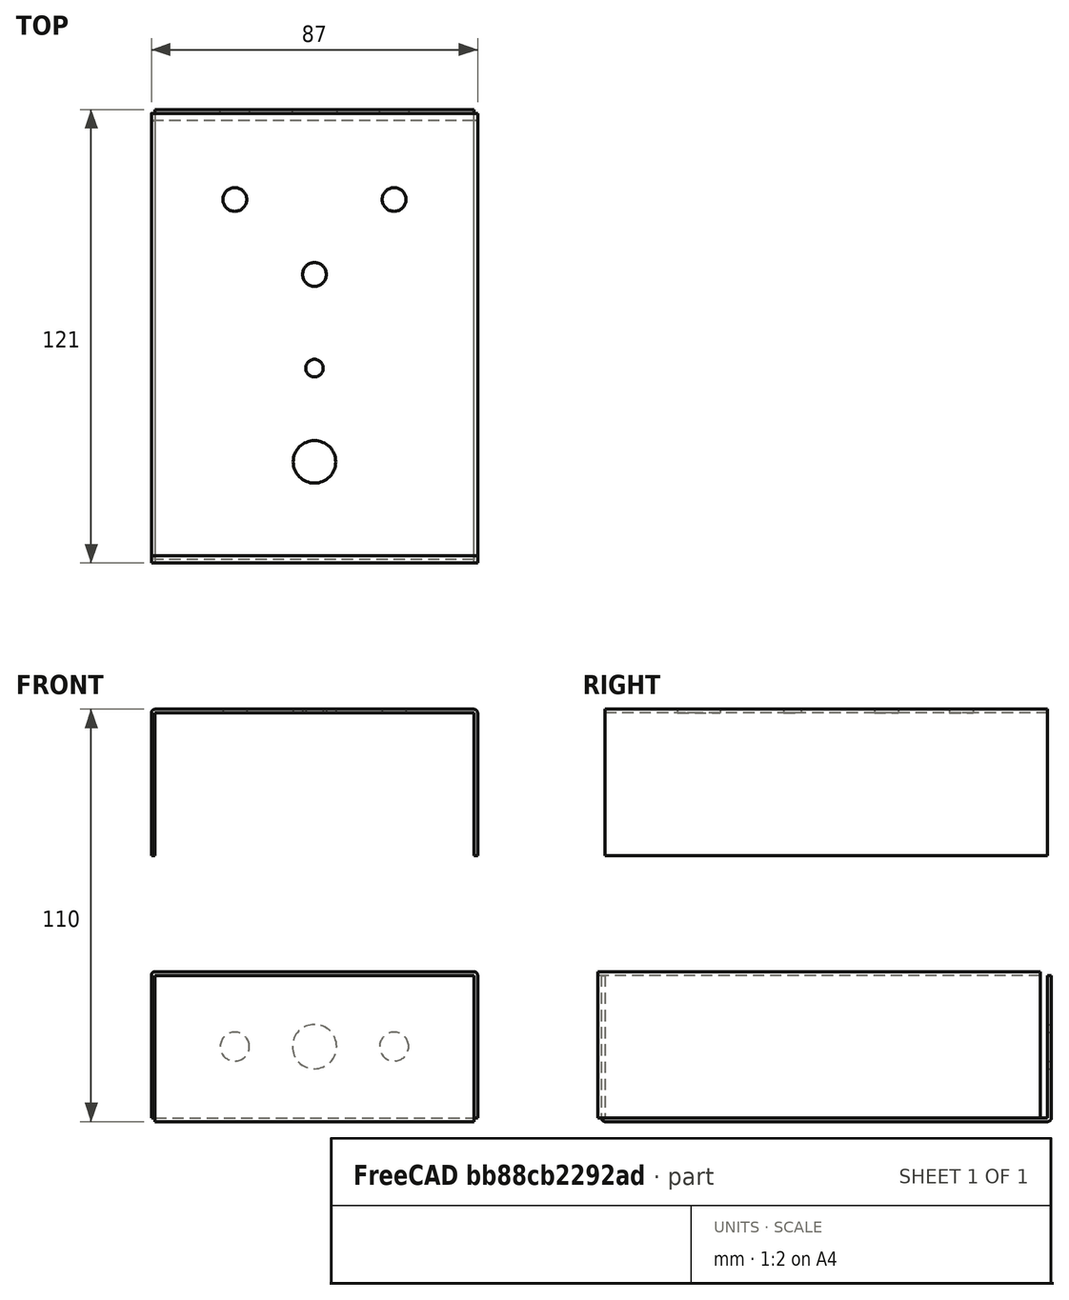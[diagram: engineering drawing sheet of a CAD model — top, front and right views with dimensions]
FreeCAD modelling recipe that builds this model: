
FCSTD DOCUMENT  (FreeCAD 0.21R33771 (Git))
Label: Trino1
License: All rights reserved
LicenseURL: http://en.wikipedia.org/wiki/All_rights_reserved
objects: TechDraw::DrawViewDimension×20, TechDraw::DrawProjGroupItem×14, Sketcher::SketchObject×5, PartDesign::Pad×3, PartDesign::Thickness×3, PartDesign::Body×3, PartDesign::Hole×3, TechDraw::DrawSVGTemplate×2, TechDraw::DrawProjGroup×2, TechDraw::DrawPage×2, PartDesign::ShapeBinder×1, App::FeaturePython×1, PartDesign::Pocket×1
note: 61 computed .brp shape members not serialized (recipe doc carries the construction recipe); baked Part::Feature solids carry a one-line shape summary decoded from their .brp

FEATURE [Sketcher::SketchObject] Sketch
  FullyConstrained = true
  MapMode = 5
  Support = -> [XY_Plane]
  sketch-geometry (4):
    g0: LineSegment StartX=0 StartY=118 StartZ=0 EndX=0 EndY=0 EndZ=0
    g1: LineSegment StartX=0 StartY=0 StartZ=0 EndX=85 EndY=0 EndZ=0
    g2: LineSegment StartX=85 StartY=0 StartZ=0 EndX=85 EndY=118 EndZ=0
    g3: LineSegment StartX=85 StartY=118 StartZ=0 EndX=0 EndY=118 EndZ=0
  constraints (11):
    c: Coincident(g0,g1)
    c: Coincident(g1,g2)
    c: Vertical(g2)
    c: Coincident(g2,g3)
    c: Coincident(g3,g0)
    c: Vertical(g0)
    c: Horizontal(g3)
    c: Horizontal(g1)
    c: DistanceY(g2,g2) = 118
    c: DistanceX(g3,g3) = 85
    c: Coincident(g0,g-1)
FEATURE [PartDesign::Pad] Pad
  Direction = (0,0,1)
  Length = 38
  Length2 = 10
  Profile = -> Sketch
  ReferenceAxis = -> Sketch [N_Axis]
  Type = 0
FEATURE [Sketcher::SketchObject] Sketch002
  FullyConstrained = true
  MapMode = 5
  Support = -> [XY_Plane001]
  sketch-geometry (4):
    g0: LineSegment StartX=0 StartY=118 StartZ=0 EndX=0 EndY=0 EndZ=0
    g1: LineSegment StartX=0 StartY=0 StartZ=0 EndX=85 EndY=0 EndZ=0
    g2: LineSegment StartX=85 StartY=0 StartZ=0 EndX=85 EndY=118 EndZ=0
    g3: LineSegment StartX=85 StartY=118 StartZ=0 EndX=0 EndY=118 EndZ=0
  constraints (11):
    c: Coincident(g0,g1)
    c: Coincident(g1,g2)
    c: Vertical(g2)
    c: Coincident(g2,g3)
    c: Coincident(g3,g0)
    c: Vertical(g0)
    c: Horizontal(g3)
    c: Horizontal(g1)
    c: DistanceY(g2,g2) = 118
    c: DistanceX(g3,g3) = 85
    c: Coincident(g0,g-1)
FEATURE [PartDesign::Pad] Pad001
  Direction = (0,0,1)
  Length = 38
  Length2 = 10
  Profile = -> Sketch002
  ReferenceAxis = -> Sketch002 [N_Axis]
  Type = 0
FEATURE [PartDesign::Thickness] Thickness001
  Base = -> Pad001 [Face3,Face5,Face1]
  BaseFeature = -> Pad001
  Intersection = false
  Join = 0
  Mode = 0
  SupportTransform = false
  Value = 1
FEATURE [PartDesign::ShapeBinder] CopyThickness
  Placement = pos=(0,0,38) rot=(0,0,1;0rad)
  TraceSupport = false
FEATURE [PartDesign::Thickness] Thickness
  Base = -> Pad [Face4,Face5,Face2]
  BaseFeature = -> Pad
  Intersection = false
  Join = 0
  Mode = 0
  SupportTransform = false
  Value = 1
FEATURE [Sketcher::SketchObject] Sketch006
  FullyConstrained = true
  MapMode = 5
  Support = -> [XY_Plane002]
  sketch-geometry (4):
    g0: LineSegment StartX=0 StartY=118 StartZ=0 EndX=0 EndY=0 EndZ=0
    g1: LineSegment StartX=0 StartY=0 StartZ=0 EndX=85 EndY=0 EndZ=0
    g2: LineSegment StartX=85 StartY=0 StartZ=0 EndX=85 EndY=118 EndZ=0
    g3: LineSegment StartX=85 StartY=118 StartZ=0 EndX=0 EndY=118 EndZ=0
  constraints (11):
    c: Coincident(g0,g1)
    c: Coincident(g1,g2)
    c: Vertical(g2)
    c: Coincident(g2,g3)
    c: Coincident(g3,g0)
    c: Vertical(g0)
    c: Horizontal(g3)
    c: Horizontal(g1)
    c: DistanceY(g2,g2) = 118
    c: DistanceX(g3,g3) = 85
    c: Coincident(g0,g-1)
FEATURE [PartDesign::Pad] Pad002
  Direction = (0,0,1)
  Length = 38
  Length2 = 10
  Profile = -> Sketch006
  ReferenceAxis = -> Sketch006 [N_Axis]
  Type = 0
FEATURE [PartDesign::Thickness] Thickness002
  Base = -> Pad002 [Face4,Face5,Face2]
  BaseFeature = -> Pad002
  Intersection = false
  Join = 0
  Mode = 0
  SupportTransform = false
  Value = 1
FEATURE [PartDesign::Body] Body002  label="Cover M"
  Group = -> [Sketch006,Pad002,Thickness002]
  Origin = -> Origin002
  Placement = pos=(0,0,-38) rot=(0,0,1;0rad)
  Tip = -> Thickness002
FEATURE [App::FeaturePython] Dimension  # Draft dimension (typed FeaturePython)
  Diameter = false
  Dimline = (101.031,14.6326,1)
  Direction = (0,0,0)
  Distance = 85
  End = (85,0,39)
  LinkedGeometry = -> [Thickness002]
  Normal = (0,0,1)
  Start = (0,0,39)
  Support = -> Thickness002
FEATURE [Sketcher::SketchObject] Sketch007
  FullyConstrained = true
  MapMode = 5
  Placement = pos=(0,0,39) rot=(0,0,1;0rad)
  Support = -> [Thickness]
  sketch-geometry (5):
    g0: Circle CenterX=21.25 CenterY=95 CenterZ=0 NormalX=0 NormalY=0 NormalZ=1 AngleXU=0 Radius=3.175
    g1: Circle CenterX=42.5 CenterY=75 CenterZ=0 NormalX=0 NormalY=0 NormalZ=1 AngleXU=0 Radius=3.175
    g2: Circle CenterX=63.75 CenterY=95 CenterZ=0 NormalX=0 NormalY=0 NormalZ=1 AngleXU=0 Radius=3.175
    g3: Circle CenterX=42.5 CenterY=25 CenterZ=0 NormalX=0 NormalY=0 NormalZ=1 AngleXU=0 Radius=5.675
    g4: Circle CenterX=42.5 CenterY=50 CenterZ=0 NormalX=0 NormalY=0 NormalZ=1 AngleXU=0 Radius=2.35
  constraints (15):
    c: Diameter(g0) = 6.35
    c: DistanceY(g-1,g0) = 95
    c: DistanceX(g-1,g0) = 21.25
    c: Diameter(g1) = 6.35
    c: DistanceX(g0,g1) = 21.25
    c: Diameter(g2) = 6.35
    c: DistanceX(g1,g2) = 21.25
    c: DistanceY(g-1,g1) = 75
    c: DistanceY(g-1,g2) = 95
    c: Diameter(g3) = 11.35
    c: DistanceY(g-1,g3) = 25
    c: DistanceX(g-1,g3) = 42.5
    c: Diameter(g4) = 4.7
    c: DistanceX(g-1,g4) = 42.5
    c: DistanceY(g4) = 50
FEATURE [Sketcher::SketchObject] Sketch008
  FullyConstrained = true
  MapMode = 5
  Placement = pos=(0,-1,0) rot=(1,0,0;1.5708rad)
  Support = -> [Thickness001]
  sketch-geometry (3):
    g0: Circle CenterX=63.75 CenterY=19 CenterZ=0 NormalX=0 NormalY=0 NormalZ=1 AngleXU=0 Radius=3.875
    g1: Circle CenterX=21.25 CenterY=19 CenterZ=0 NormalX=0 NormalY=0 NormalZ=1 AngleXU=0 Radius=3.875
    g2: Circle CenterX=42.5 CenterY=19 CenterZ=0 NormalX=0 NormalY=0 NormalZ=1 AngleXU=0 Radius=5.9
  constraints (9):
    c: Diameter(g0) = 7.75
    c: Diameter(g1) = 7.75
    c: Diameter(g2) = 11.8
    c: DistanceX(g-1,g1) = 21.25
    c: DistanceX(g-1,g0) = 63.75
    c: DistanceX(g-1,g2) = 42.5
    c: DistanceY(g-1,g2) = 19
    c: DistanceY(g-1,g1) = 19
    c: DistanceY(g-1,g0) = 19
FEATURE [PartDesign::Pocket] Pocket
  BaseFeature = -> Thickness001
  Direction = (0,1,-2e-16)
  Length = 5
  Length2 = 5
  Profile = -> Sketch008
  ReferenceAxis = -> Sketch008 [N_Axis]
  Type = 0
FEATURE [PartDesign::Body] Body001  label="Base"
  Group = -> [Sketch002,Pad001,Thickness001,CopyThickness,Sketch008,Pocket]
  Origin = -> Origin001
  Placement = pos=(0,120,-1.4e-14) rot=(1,0,0;3.14159rad)
  Tip = -> Pocket
FEATURE [PartDesign::Hole] Hole
  BaseFeature = -> Thickness
  CustomThreadClearance = 0
  Depth = 25
  DepthType = 0
  Diameter = 4.7
  DrillForDepth = false
  DrillPoint = 1
  DrillPointAngle = 118
  HoleCutCountersinkAngle = 90
  HoleCutCustomValues = false
  HoleCutDepth = 0
  HoleCutDiameter = 6.1
  HoleCutType = 0
  ModelThread = false
  Profile = -> Sketch007
  Tapered = false
  TaperedAngle = 90
  ThreadClass = 0
  ThreadDepth = 25
  ThreadDepthType = 0
  ThreadDirection = 0
  ThreadFit = 0
  ThreadSize = 0
  ThreadType = 0
  Threaded = false
  UseCustomThreadClearance = false
FEATURE [PartDesign::Hole] Hole001
  BaseFeature = -> Hole
  CustomThreadClearance = 0
  Depth = 25
  DepthType = 0
  Diameter = 6.35
  DrillForDepth = false
  DrillPoint = 1
  DrillPointAngle = 118
  HoleCutCountersinkAngle = 90
  HoleCutCustomValues = false
  HoleCutDepth = 0
  HoleCutDiameter = 6.1
  HoleCutType = 0
  ModelThread = false
  Profile = -> Hole [Edge38,Edge39,Edge37]
  Tapered = false
  TaperedAngle = 90
  ThreadClass = 0
  ThreadDepth = 25
  ThreadDepthType = 0
  ThreadDirection = 0
  ThreadFit = 0
  ThreadSize = 0
  ThreadType = 0
  Threaded = false
  UseCustomThreadClearance = false
FEATURE [PartDesign::Hole] Hole002
  BaseFeature = -> Hole001
  CustomThreadClearance = 0
  Depth = 25
  DepthType = 0
  Diameter = 11.35
  DrillForDepth = false
  DrillPoint = 1
  DrillPointAngle = 118
  HoleCutCountersinkAngle = 90
  HoleCutCustomValues = false
  HoleCutDepth = 0
  HoleCutDiameter = 0
  HoleCutType = 0
  ModelThread = false
  Profile = -> Hole001 [Edge35]
  Tapered = false
  TaperedAngle = 90
  ThreadClass = 0
  ThreadDepth = 25
  ThreadDepthType = 0
  ThreadDirection = 0
  ThreadFit = 0
  ThreadSize = 0
  ThreadType = 0
  Threaded = false
  UseCustomThreadClearance = false
FEATURE [PartDesign::Body] Body  label="Cover"
  Group = -> [Sketch,Pad,Thickness,Sketch007,Hole,Hole001,Hole002]
  Origin = -> Origin
  Placement = pos=(6.1e-14,2,32) rot=(0,0,1;0rad)
  Tip = -> Hole002
FEATURE [TechDraw::DrawSVGTemplate] Template001
  EditableTexts = AUTHOR_NAME=Corvalán, Abel; DN=N2; DRAWING_TITLE=Trino Base Enclousure; FC-DATE=09/03/2025; FC-REV=REV A; FC-SC=1:2; FC-SH=1/1; FC-SI=A3; FreeCAD_DRAWING=FreeCAD DRAWING; PN=N2
  Height = 297
  Orientation = 1
  Template = /app/share/Mod/TechDraw/Templates/A3_Landscape_ISO7200TD.svg
  Width = 420
FEATURE [TechDraw::DrawProjGroupItem] ProjItem015  label="Front002"
  CoarseView = false
  Direction = (-1.3e-15,0,-1)
  Focus = 100
  HardHidden = false
  IsoCount = 0
  IsoHidden = false
  IsoVisible = false
  LockPosition = true
  Perspective = false
  Rotation = 0
  RotationVector = (1,0,0)
  Scale = 0.5
  ScaleType = 2
  ScrubCount = 0
  SeamHidden = false
  SeamVisible = false
  SmoothHidden = false
  SmoothVisible = true
  Source = -> [Pocket]
  Type = 0
  X = 0
  XDirection = (1,0,-1.3e-15)
  Y = 0
FEATURE [TechDraw::DrawProjGroupItem] ProjItem017  label="Bottom002"
  CoarseView = false
  Direction = (0,1,0)
  Focus = 100
  HardHidden = false
  IsoCount = 0
  IsoHidden = false
  IsoVisible = false
  LockPosition = false
  Perspective = false
  Rotation = 0
  RotationVector = (1,0,0)
  ScaleType = 2
  ScrubCount = 0
  SeamHidden = false
  SeamVisible = false
  SmoothHidden = false
  SmoothVisible = true
  Source = -> [Pocket]
  Type = 5
  X = 0
  XDirection = (1,0,-1.3e-15)
  Y = 69.75
FEATURE [TechDraw::DrawProjGroupItem] ProjItem018  label="Left002"
  CoarseView = false
  Direction = (-1,0,1.2e-15)
  Focus = 100
  HardHidden = false
  IsoCount = 0
  IsoHidden = false
  IsoVisible = false
  LockPosition = false
  Perspective = false
  Rotation = 0
  RotationVector = (1,0,0)
  ScaleType = 2
  ScrubCount = 0
  SeamHidden = false
  SeamVisible = false
  SmoothHidden = false
  SmoothVisible = true
  Source = -> [Pocket]
  Type = 1
  X = 73.1703
  XDirection = (-1.2e-15,0,-1)
  Y = 0
FEATURE [TechDraw::DrawProjGroupItem] ProjItem019  label="Top002"
  CoarseView = false
  Direction = (0,-1,0)
  Focus = 100
  HardHidden = false
  IsoCount = 0
  IsoHidden = false
  IsoVisible = false
  LockPosition = false
  Perspective = false
  Rotation = 0
  RotationVector = (1,0,0)
  ScaleType = 2
  ScrubCount = 0
  SeamHidden = false
  SeamVisible = false
  SmoothHidden = false
  SmoothVisible = true
  Source = -> [Pocket]
  Type = 4
  X = 0
  XDirection = (1,0,-1.3e-15)
  Y = -97.0726
FEATURE [TechDraw::DrawProjGroupItem] ProjItem020  label="Right002"
  CoarseView = false
  Direction = (1,0,-1.4e-15)
  Focus = 100
  HardHidden = false
  IsoCount = 0
  IsoHidden = false
  IsoVisible = false
  LockPosition = false
  Perspective = false
  Rotation = 0
  RotationVector = (1,0,0)
  ScaleType = 2
  ScrubCount = 0
  SeamHidden = false
  SeamVisible = false
  SmoothHidden = false
  SmoothVisible = true
  Source = -> [Pocket]
  Type = 2
  X = -61
  XDirection = (1.4e-15,0,1)
  Y = 0
FEATURE [TechDraw::DrawProjGroupItem] ProjItem021  label="Rear001"
  CoarseView = false
  Direction = (1.3e-15,0,1)
  Focus = 100
  HardHidden = false
  IsoCount = 0
  IsoHidden = false
  IsoVisible = false
  LockPosition = false
  Perspective = false
  Rotation = 0
  RotationVector = (1,0,0)
  ScaleType = 2
  ScrubCount = 0
  SeamHidden = false
  SeamVisible = false
  SmoothHidden = false
  SmoothVisible = true
  Source = -> [Pocket]
  Type = 3
  X = 146.341
  XDirection = (-1,0,1.3e-15)
  Y = 0
FEATURE [TechDraw::DrawProjGroupItem] ProjItem022  label="FrontTopLeft"
  CoarseView = false
  Direction = (-0.57735,-0.57735,-0.57735)
  Focus = 100
  HardHidden = false
  IsoCount = 0
  IsoHidden = false
  IsoVisible = false
  LockPosition = false
  Perspective = false
  Rotation = 0
  RotationVector = (1,0,0)
  ScaleType = 2
  ScrubCount = 0
  SeamHidden = false
  SeamVisible = false
  SmoothHidden = false
  SmoothVisible = true
  Source = -> [Pocket]
  Type = 6
  X = 73.1703
  XDirection = (0.707107,0,-0.707107)
  Y = -97.0726
FEATURE [TechDraw::DrawProjGroup] ProjGroup002
  Anchor = -> ProjItem015
  AutoDistribute = true
  LockPosition = false
  ProjectionType = 0
  Rotation = 0
  Scale = 0.5
  ScaleType = 2
  Source = -> [Pocket]
  Views = -> [ProjItem015,ProjItem017,ProjItem018,ProjItem019,ProjItem020,ProjItem021,ProjItem022]
  X = 134.039
  Y = 155.977
  spacingX = 30
  spacingY = 30
FEATURE [TechDraw::DrawViewDimension] Dimension007
  AngleOverride = false
  Arbitrary = false
  ArbitraryTolerances = false
  EqualTolerance = true
  ExtensionAngle = 0
  FormatSpec = ⌀%.2w
  FormatSpecOverTolerance = %+.2w
  FormatSpecUnderTolerance = %+.2w
  Inverted = false
  LineAngle = 0
  LockPosition = false
  MeasureType = 1
  OverTolerance = 0
  References2D = -> [ProjItem019]
  Rotation = 0
  ScaleType = 0
  TheoreticalExact = false
  Type = 5
  UnderTolerance = 0
  X = -22.8292
  Y = -17.8757
FEATURE [TechDraw::DrawViewDimension] Dimension008
  AngleOverride = false
  Arbitrary = false
  ArbitraryTolerances = false
  EqualTolerance = true
  ExtensionAngle = 0
  FormatSpec = 2x⌀%.2w
  FormatSpecOverTolerance = %+.2w
  FormatSpecUnderTolerance = %+.2w
  Inverted = false
  LineAngle = 0
  LockPosition = false
  MeasureType = 1
  OverTolerance = 0
  References2D = -> [ProjItem019]
  Rotation = 0
  ScaleType = 0
  TheoreticalExact = false
  Type = 5
  UnderTolerance = 0
  X = -36.3975
  Y = -21.3216
FEATURE [TechDraw::DrawViewDimension] Dimension010
  AngleOverride = false
  Arbitrary = false
  ArbitraryTolerances = false
  EqualTolerance = true
  ExtensionAngle = 0
  FormatSpec = %.2w
  FormatSpecOverTolerance = %+.2w
  FormatSpecUnderTolerance = %+.2w
  Inverted = false
  LineAngle = 0
  LockPosition = false
  MeasureType = 1
  OverTolerance = 0
  References2D = -> [ProjItem015]
  Rotation = 0
  ScaleType = 0
  TheoreticalExact = false
  Type = 1
  UnderTolerance = 0
  X = 0.410694
  Y = 50.166
FEATURE [TechDraw::DrawViewDimension] Dimension011
  AngleOverride = false
  Arbitrary = false
  ArbitraryTolerances = false
  EqualTolerance = true
  ExtensionAngle = 0
  FormatSpec = %.2w
  FormatSpecOverTolerance = %+.2w
  FormatSpecUnderTolerance = %+.2w
  Inverted = false
  LineAngle = 0
  LockPosition = false
  MeasureType = 1
  OverTolerance = 0
  References2D = -> [ProjItem015]
  Rotation = 0
  ScaleType = 0
  TheoreticalExact = false
  Type = 2
  UnderTolerance = 0
  X = 28.7879
  Y = 1.85389
FEATURE [TechDraw::DrawViewDimension] Dimension012
  AngleOverride = false
  Arbitrary = false
  ArbitraryTolerances = false
  EqualTolerance = true
  ExtensionAngle = 0
  FormatSpec = %.2w
  FormatSpecOverTolerance = %+.2w
  FormatSpecUnderTolerance = %+.2w
  Inverted = false
  LineAngle = 0
  LockPosition = false
  MeasureType = 1
  OverTolerance = 0
  References2D = -> [ProjItem018]
  Rotation = 0
  ScaleType = 0
  TheoreticalExact = false
  Type = 1
  UnderTolerance = 0
  X = -0.396109
  Y = 48.0066
FEATURE [TechDraw::DrawViewDimension] Dimension015
  AngleOverride = false
  Arbitrary = false
  ArbitraryTolerances = false
  EqualTolerance = true
  ExtensionAngle = 0
  FormatSpec = %.2w
  FormatSpecOverTolerance = %+.2w
  FormatSpecUnderTolerance = %+.2w
  Inverted = false
  LineAngle = 0
  LockPosition = false
  MeasureType = 1
  OverTolerance = 0
  References2D = -> [ProjItem019]
  Rotation = 0
  ScaleType = 0
  TheoreticalExact = false
  Type = 1
  UnderTolerance = 0
  X = -34.1053
  Y = 30.5157
FEATURE [TechDraw::DrawViewDimension] Dimension016
  AngleOverride = false
  Arbitrary = false
  ArbitraryTolerances = false
  EqualTolerance = true
  ExtensionAngle = 0
  FormatSpec = %.2w
  FormatSpecOverTolerance = %+.2w
  FormatSpecUnderTolerance = %+.2w
  Inverted = false
  LineAngle = 0
  LockPosition = false
  MeasureType = 1
  OverTolerance = 0
  References2D = -> [ProjItem019]
  Rotation = 0
  ScaleType = 0
  TheoreticalExact = false
  Type = 1
  UnderTolerance = 0
  X = -34.3392
  Y = 21.745
FEATURE [TechDraw::DrawViewDimension] Dimension017
  AngleOverride = false
  Arbitrary = false
  ArbitraryTolerances = false
  EqualTolerance = true
  ExtensionAngle = 0
  FormatSpec = %.2w
  FormatSpecOverTolerance = %+.2w
  FormatSpecUnderTolerance = %+.2w
  Inverted = false
  LineAngle = 0
  LockPosition = false
  MeasureType = 1
  OverTolerance = 0
  References2D = -> [ProjItem019]
  Rotation = 0
  ScaleType = 0
  TheoreticalExact = false
  Type = 1
  UnderTolerance = 0
  X = -6.87869
  Y = 38.0334
FEATURE [TechDraw::DrawPage] Page001  label="Base Page"
  KeepUpdated = true
  NextBalloonIndex = 1
  ProjectionType = 0
  Template = -> Template001
  Views = -> [ProjGroup002,Dimension007,Dimension008,Dimension010,Dimension011,Dimension012,Dimension015,Dimension016,Dimension017]
FEATURE [TechDraw::DrawSVGTemplate] Template
  EditableTexts = AUTHOR_NAME=Corvalán, Abel; DN=N1; DRAWING_TITLE=Trino Cover Enclousure; FC-DATE=10/03/2025; FC-REV=REV A; FC-SC=1:2; FC-SH=1/1; FC-SI=A3; FreeCAD_DRAWING=FreeCAD DRAWING; PN=N1
  Height = 297
  Orientation = 1
  Template = /app/share/Mod/TechDraw/Templates/A3_Landscape_ISO7200TD.svg
  Width = 420
FEATURE [TechDraw::DrawProjGroupItem] ProjItem  label="Front"
  CoarseView = false
  Direction = (0,0,1)
  Focus = 100
  HardHidden = false
  IsoCount = 0
  IsoHidden = false
  IsoVisible = false
  LockPosition = true
  Perspective = false
  Rotation = 0
  RotationVector = (1,0,0)
  Scale = 0.5
  ScaleType = 2
  ScrubCount = 0
  SeamHidden = false
  SeamVisible = false
  SmoothHidden = false
  SmoothVisible = true
  Source = -> [Hole002]
  Type = 0
  X = 0
  XDirection = (1,0,0)
  Y = 0
FEATURE [TechDraw::DrawProjGroupItem] ProjItem023  label="Left"
  CoarseView = false
  Direction = (-1,0,1e-16)
  Focus = 100
  HardHidden = false
  IsoCount = 0
  IsoHidden = false
  IsoVisible = false
  LockPosition = false
  Perspective = false
  Rotation = 0
  RotationVector = (1,0,0)
  Scale = 0.5
  ScaleType = 2
  ScrubCount = 0
  SeamHidden = false
  SeamVisible = false
  SmoothHidden = false
  SmoothVisible = true
  Source = -> [Hole002]
  Type = 1
  X = -73.9203
  XDirection = (1e-16,0,1)
  Y = 0
FEATURE [TechDraw::DrawProjGroupItem] ProjItem024  label="Right"
  CoarseView = false
  Direction = (1,0,1e-16)
  Focus = 100
  HardHidden = false
  IsoCount = 0
  IsoHidden = false
  IsoVisible = false
  LockPosition = false
  Perspective = false
  Rotation = 0
  RotationVector = (1,0,0)
  Scale = 0.5
  ScaleType = 2
  ScrubCount = 0
  SeamHidden = false
  SeamVisible = false
  SmoothHidden = false
  SmoothVisible = true
  Source = -> [Hole002]
  Type = 2
  X = 61.5
  XDirection = (1e-16,0,-1)
  Y = 0
FEATURE [TechDraw::DrawProjGroupItem] ProjItem025  label="Bottom"
  CoarseView = false
  Direction = (0,-1,0)
  Focus = 100
  HardHidden = false
  IsoCount = 0
  IsoHidden = false
  IsoVisible = false
  LockPosition = false
  Perspective = false
  Rotation = 0
  RotationVector = (1,0,0)
  Scale = 0.5
  ScaleType = 2
  ScrubCount = 0
  SeamHidden = false
  SeamVisible = false
  SmoothHidden = false
  SmoothVisible = true
  Source = -> [Hole002]
  Type = 5
  X = 0
  XDirection = (1,0,0)
  Y = -69.25
FEATURE [TechDraw::DrawProjGroupItem] ProjItem026  label="Top"
  CoarseView = false
  Direction = (0,1,0)
  Focus = 100
  HardHidden = false
  IsoCount = 0
  IsoHidden = false
  IsoVisible = false
  LockPosition = false
  Perspective = false
  Rotation = 0
  RotationVector = (1,0,0)
  Scale = 0.5
  ScaleType = 2
  ScrubCount = 0
  SeamHidden = false
  SeamVisible = false
  SmoothHidden = false
  SmoothVisible = true
  Source = -> [Hole002]
  Type = 4
  X = 0
  XDirection = (1,0,0)
  Y = 96.3867
FEATURE [TechDraw::DrawProjGroupItem] ProjItem027  label="FrontTopLeft001"
  CoarseView = false
  Direction = (-0.57735,0.57735,0.57735)
  Focus = 100
  HardHidden = false
  IsoCount = 0
  IsoHidden = false
  IsoVisible = false
  LockPosition = false
  Perspective = false
  Rotation = 0
  RotationVector = (1,0,0)
  ScaleType = 2
  ScrubCount = 0
  SeamHidden = false
  SeamVisible = false
  SmoothHidden = false
  SmoothVisible = true
  Source = -> [Hole002]
  Type = 6
  X = -73.9203
  XDirection = (0.707107,0,0.707107)
  Y = 96.3867
FEATURE [TechDraw::DrawProjGroupItem] ProjItem028  label="Rear"
  CoarseView = false
  Direction = (0,0,-1)
  Focus = 100
  HardHidden = false
  IsoCount = 0
  IsoHidden = false
  IsoVisible = false
  LockPosition = false
  Perspective = false
  Rotation = 0
  RotationVector = (1,0,0)
  ScaleType = 2
  ScrubCount = 0
  SeamHidden = false
  SeamVisible = false
  SmoothHidden = false
  SmoothVisible = true
  Source = -> [Hole002]
  Type = 3
  X = 123
  XDirection = (-1,0,0)
  Y = 0
FEATURE [TechDraw::DrawProjGroup] ProjGroup
  Anchor = -> ProjItem
  AutoDistribute = true
  LockPosition = false
  ProjectionType = 1
  Rotation = 0
  Scale = 0.5
  ScaleType = 2
  Source = -> [Hole002]
  Views = -> [ProjItem,ProjItem023,ProjItem024,ProjItem025,ProjItem026,ProjItem027,ProjItem028]
  X = 134.402
  Y = 136.406
  spacingX = 30
  spacingY = 30
FEATURE [TechDraw::DrawViewDimension] Dimension018
  AngleOverride = false
  Arbitrary = false
  ArbitraryTolerances = false
  EqualTolerance = true
  ExtensionAngle = 0
  FormatSpec = %.2w
  FormatSpecOverTolerance = %+.2w
  FormatSpecUnderTolerance = %+.2w
  Inverted = false
  LineAngle = 0
  LockPosition = false
  MeasureType = 1
  OverTolerance = 0
  References2D = -> [ProjItem]
  Rotation = 0
  ScaleType = 0
  TheoreticalExact = false
  Type = 1
  UnderTolerance = 0
  X = -0.725123
  Y = 66.2905
FEATURE [TechDraw::DrawViewDimension] Dimension019
  AngleOverride = false
  Arbitrary = false
  ArbitraryTolerances = false
  EqualTolerance = true
  ExtensionAngle = 0
  FormatSpec = %.2w
  FormatSpecOverTolerance = %+.2w
  FormatSpecUnderTolerance = %+.2w
  Inverted = false
  LineAngle = 0
  LockPosition = false
  MeasureType = 1
  OverTolerance = 0
  References2D = -> [ProjItem]
  Rotation = 0
  ScaleType = 0
  TheoreticalExact = false
  Type = 2
  UnderTolerance = 0
  X = -54.1536
  Y = 3.32831
FEATURE [TechDraw::DrawViewDimension] Dimension023
  AngleOverride = false
  Arbitrary = false
  ArbitraryTolerances = false
  EqualTolerance = true
  ExtensionAngle = 0
  FormatSpec = ⌀%.2w
  FormatSpecOverTolerance = %+.2w
  FormatSpecUnderTolerance = %+.2w
  Inverted = false
  LineAngle = 0
  LockPosition = false
  MeasureType = 1
  OverTolerance = 0.3
  References2D = -> [ProjItem]
  Rotation = 0
  ScaleType = 0
  TheoreticalExact = false
  Type = 5
  UnderTolerance = -0.3
  X = 35.5399
  Y = -18.0915
FEATURE [TechDraw::DrawViewDimension] Dimension024
  AngleOverride = false
  Arbitrary = false
  ArbitraryTolerances = false
  EqualTolerance = true
  ExtensionAngle = 0
  FormatSpec = ⌀%.2w
  FormatSpecOverTolerance = %+.2w
  FormatSpecUnderTolerance = %+.2w
  Inverted = false
  LineAngle = 0
  LockPosition = false
  MeasureType = 1
  OverTolerance = 0
  References2D = -> [ProjItem]
  Rotation = 0
  ScaleType = 0
  TheoreticalExact = false
  Type = 5
  UnderTolerance = 0
  X = 32.7787
  Y = -28.7651
FEATURE [TechDraw::DrawViewDimension] Dimension025
  AngleOverride = false
  Arbitrary = false
  ArbitraryTolerances = false
  EqualTolerance = true
  ExtensionAngle = 0
  FormatSpec = %.2w
  FormatSpecOverTolerance = %+.2w
  FormatSpecUnderTolerance = %+.2w
  Inverted = false
  LineAngle = 0
  LockPosition = false
  MeasureType = 1
  OverTolerance = 0
  References2D = -> [ProjItem]
  Rotation = 0
  ScaleType = 0
  TheoreticalExact = false
  Type = 2
  UnderTolerance = 0
  X = -33.7597
  Y = 16.2055
FEATURE [TechDraw::DrawViewDimension] Dimension026
  AngleOverride = false
  Arbitrary = false
  ArbitraryTolerances = false
  EqualTolerance = true
  ExtensionAngle = 0
  FormatSpec = %.2w
  FormatSpecOverTolerance = %+.2w
  FormatSpecUnderTolerance = %+.2w
  Inverted = false
  LineAngle = 0
  LockPosition = false
  MeasureType = 1
  OverTolerance = 0
  References2D = -> [ProjItem]
  Rotation = 0
  ScaleType = 0
  TheoreticalExact = false
  Type = 2
  UnderTolerance = 0
  X = -33.7913
  Y = 4.61141
FEATURE [TechDraw::DrawViewDimension] Dimension027
  AngleOverride = false
  Arbitrary = false
  ArbitraryTolerances = false
  EqualTolerance = true
  ExtensionAngle = 0
  FormatSpec = %.2w
  FormatSpecOverTolerance = %+.2w
  FormatSpecUnderTolerance = %+.2w
  Inverted = false
  LineAngle = 0
  LockPosition = false
  MeasureType = 1
  OverTolerance = 0
  References2D = -> [ProjItem]
  Rotation = 0
  ScaleType = 0
  TheoreticalExact = false
  Type = 2
  UnderTolerance = 0
  X = -34.001
  Y = -21.2317
FEATURE [TechDraw::DrawViewDimension] Dimension028
  AngleOverride = false
  Arbitrary = false
  ArbitraryTolerances = false
  EqualTolerance = true
  ExtensionAngle = 0
  FormatSpec = %.2w
  FormatSpecOverTolerance = %+.2w
  FormatSpecUnderTolerance = %+.2w
  Inverted = false
  LineAngle = 0
  LockPosition = false
  MeasureType = 1
  OverTolerance = 0
  References2D = -> [ProjItem]
  Rotation = 0
  ScaleType = 0
  TheoreticalExact = false
  Type = 2
  UnderTolerance = 0
  X = -33.7657
  Y = 26.25
FEATURE [TechDraw::DrawViewDimension] Dimension029
  AngleOverride = false
  Arbitrary = false
  ArbitraryTolerances = false
  EqualTolerance = true
  ExtensionAngle = 0
  FormatSpec = %.2w
  FormatSpecOverTolerance = %+.2w
  FormatSpecUnderTolerance = %+.2w
  Inverted = false
  LineAngle = 0
  LockPosition = false
  MeasureType = 1
  OverTolerance = 0
  References2D = -> [ProjItem024]
  Rotation = 0
  ScaleType = 0
  TheoreticalExact = false
  Type = 1
  UnderTolerance = 0
  X = -0.971929
  Y = 52.4254
FEATURE [TechDraw::DrawViewDimension] Dimension030
  AngleOverride = false
  Arbitrary = false
  ArbitraryTolerances = false
  EqualTolerance = true
  ExtensionAngle = 0
  FormatSpec = %.2w
  FormatSpecOverTolerance = %+.2w
  FormatSpecUnderTolerance = %+.2w
  Inverted = false
  LineAngle = 0
  LockPosition = false
  MeasureType = 1
  OverTolerance = 0
  References2D = -> [ProjItem]
  Rotation = 0
  ScaleType = 0
  TheoreticalExact = false
  Type = 1
  UnderTolerance = 0
  X = -35.3438
  Y = 54.0377
FEATURE [TechDraw::DrawViewDimension] Dimension031
  AngleOverride = false
  Arbitrary = false
  ArbitraryTolerances = false
  EqualTolerance = true
  ExtensionAngle = 0
  FormatSpec = %.2w
  FormatSpecOverTolerance = %+.2w
  FormatSpecUnderTolerance = %+.2w
  Inverted = false
  LineAngle = 0
  LockPosition = false
  MeasureType = 1
  OverTolerance = 0
  References2D = -> [ProjItem]
  Rotation = 0
  ScaleType = 0
  TheoreticalExact = false
  Type = 1
  UnderTolerance = 0
  X = -0.499538
  Y = 43.9691
FEATURE [TechDraw::DrawViewDimension] Dimension032
  AngleOverride = false
  Arbitrary = false
  ArbitraryTolerances = false
  EqualTolerance = true
  ExtensionAngle = 0
  FormatSpec = 3x⌀%.2w
  FormatSpecOverTolerance = %+.2w
  FormatSpecUnderTolerance = %+.2w
  Inverted = false
  LineAngle = 0
  LockPosition = false
  MeasureType = 1
  OverTolerance = 0
  References2D = -> [ProjItem]
  Rotation = 0
  ScaleType = 0
  TheoreticalExact = false
  Type = 5
  UnderTolerance = 0
  X = 34.234
  Y = -2.7116
FEATURE [TechDraw::DrawPage] Page  label="Cover Page"
  KeepUpdated = true
  NextBalloonIndex = 1
  ProjectionType = 0
  Template = -> Template
  Views = -> [ProjGroup,Dimension018,Dimension019,Dimension023,Dimension024,Dimension025,Dimension026,Dimension027,Dimension028,Dimension029,Dimension030,Dimension031,Dimension032]
